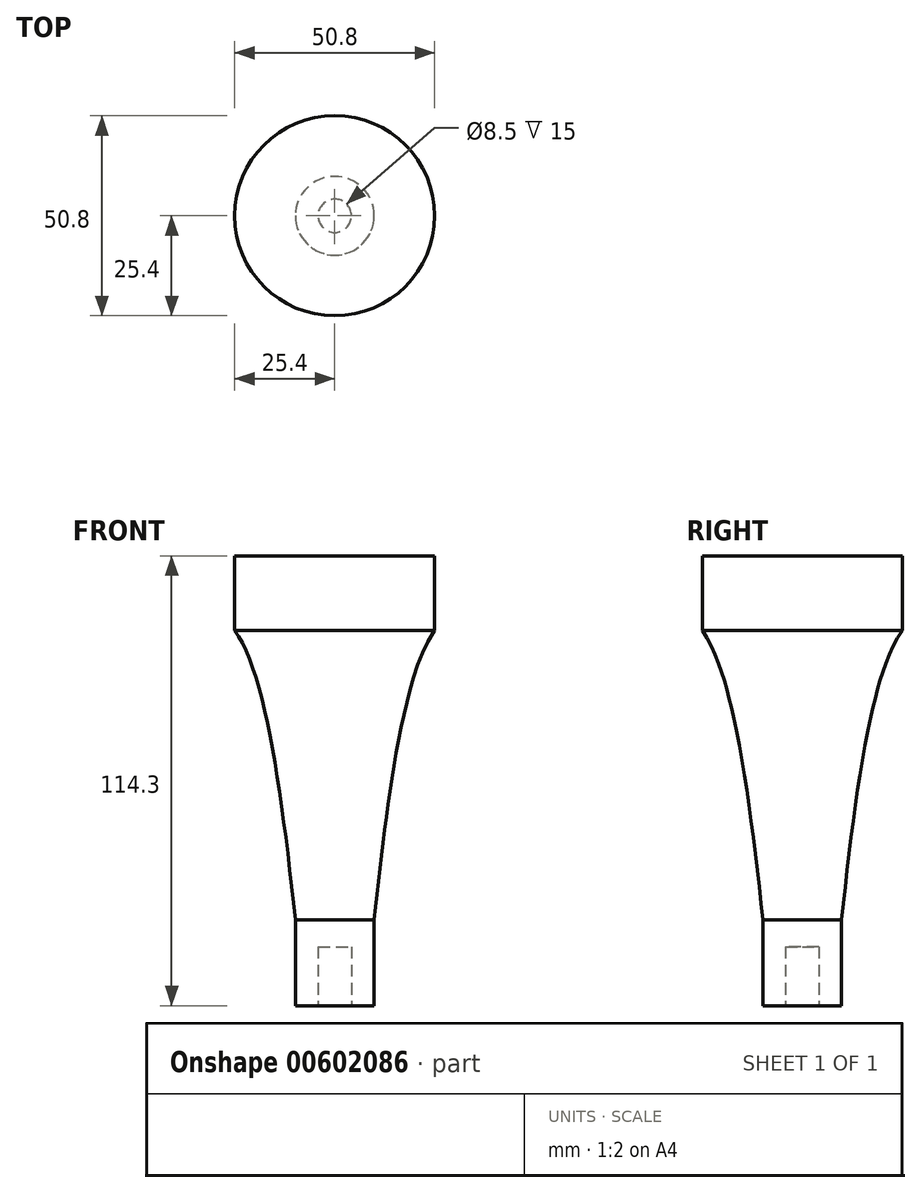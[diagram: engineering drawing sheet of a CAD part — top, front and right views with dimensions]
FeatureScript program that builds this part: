
annotation { "Feature Type Name" : "Feature", "Feature Type Description" : "" }
export const myFeature = defineFeature(function(context is Context, id is Id, definition is map)
    precondition{}
    {
        {
            var Q0;
            Q0=qCreatedBy(makeId("Top.planeOp"),FACE);
            var sketch = newSketch(context, id + "F0", { "sketchPlane" : qUnion([Q0])});
            skCircle(sketch, "E0", {"center": v(0, 0) * mm, "radius": 10 * mm});
            skSolve(sketch);
        }
        {
            var Q0;
            Q0 = qSketchRegion(id + "F0", true);
            extrude(context, id + "F1", {"entities" : qUnion([Q0]), "depth" : 101.6 * mm, "offsetDistance" : 25.4 * mm});
        }
        {
            var Q0;
            Q0=qCreatedBy(makeId("Front.planeOp"),FACE);
            var sketch = newSketch(context, id + "F2", { "sketchPlane" : qUnion([Q0])});
            skLineSegment(sketch, "E1.bottom", {"start": v(0, 0) * mm, "end": v(38.1, 0) * mm});
            skLineSegment(sketch, "E1.top", {"start": v(0, 101.6) * mm, "end": v(38.1, 101.6) * mm});
            skLineSegment(sketch, "E1.left", {"start": v(0, 0) * mm, "end": v(0, 101.6) * mm});
            skLineSegment(sketch, "E1.right", {"start": v(38.1, 0) * mm, "end": v(38.1, 101.6) * mm});
            skFitSpline(sketch, "E2", {"points": [v(38.1, 101.6) * mm, v(25.8, 95.89) * mm, v(7.77, 0) * mm], "startDerivative": vector(-48.1, -6) * mm, "endDerivative": vector(-17.25, -171.93) * mm});
            skSolve(sketch);
        }
        {
            var Q0;
            Q0=makeQuery(id+"F2.imprint","IMPRINT",FACE,{"disambiguationData":[TD([[makeQuery(id+"F2.imprint","IMPRINT",EDGE,{"derivedFrom":sQuery(id+"F2.wireOp",EDGE,"E1.top")}),-1.0]])]});
            var Q1;
            Q1=sQuery(id+"F2.wireOp",EDGE,"E1.left");
            revolve(context, id + "F3", {"operationType" : NewBodyOperationType.ADD, "entities" : qUnion([Q0]), "axis" : qUnion([Q1]), "revolveType" : RevolveType.FULL});
        }
        {
            var Q0;
            Q0=makeQuery(id+"F3.boolean.opBoolean","MERGE",FACE,{"derivedFrom":[makeQuery(id+"F1.opExtrude","CAP_FACE",FACE,{"disambiguationData":[OSD([sQuery(id+"F0.wireOp",EDGE,"E0")])],"isStart":false}),makeQuery(id+"F3.opRevolve","SWEPT_FACE",FACE,{"disambiguationData":[OSD([sQuery(id+"F2.wireOp",EDGE,"E1.top")])]})]});
            var sketch = newSketch(context, id + "F4", { "sketchPlane" : qUnion([Q0])});
            skSolve(sketch);
        }
        {
            var Q0;
            Q0 = qSketchRegion(id + "F4", true);
            var Q1;
            Q1=makeQuery(id+"F4.imprint","IMPRINT",FACE,{"disambiguationData":[TD([[makeQuery(id+"F4.imprint","IMPRINT",EDGE,{"derivedFrom":makeQuery(id+"F3.opRevolve","SWEPT_EDGE",EDGE,{"disambiguationData":[OSD([sQuery(id+"F2.wireOp",EDGE,"E1.top"),sQuery(id+"F2.wireOp",EDGE,"E1.right"),sQuery(id+"F2.wireOp",EDGE,"E2")])]})}),-1.0]])]});
            extrude(context, id + "F5", {"entities" : qUnion([Q0, Q1]), "operationType" : NewBodyOperationType.ADD, "depth" : 12.7 * mm, "offsetDistance" : 25.4 * mm});
        }
        {
            var Q0;
            Q0=makeQuery(id+"F1.opExtrude","CAP_FACE",FACE,{"disambiguationData":[OSD([sQuery(id+"F0.wireOp",EDGE,"E0")])],"isStart":true});
            var sketch = newSketch(context, id + "F6", { "sketchPlane" : qUnion([Q0])});
            skCircle(sketch, "E3", {"center": v(0, 0) * mm, "radius": 4.25 * mm});
            skSolve(sketch);
        }
        {
            var Q0;
            Q0 = qSketchRegion(id + "F6", true);
            extrude(context, id + "F7", {"entities" : qUnion([Q0]), "operationType" : NewBodyOperationType.REMOVE, "oppositeDirection" : true, "depth" : 15 * mm, "offsetDistance" : 25.4 * mm});
        }
        {
            var Q0;
            Q0=makeQuery(id+"F5.opExtrude","CAP_FACE",FACE,{"disambiguationData":[OSD([sQuery(id+"F2.wireOp",EDGE,"E1.top"),sQuery(id+"F2.wireOp",EDGE,"E1.right"),sQuery(id+"F2.wireOp",EDGE,"E2")])],"isStart":false});
            var sketch = newSketch(context, id + "F8", { "sketchPlane" : qUnion([Q0])});
            skCircle(sketch, "E4", {"center": v(0, 0) * mm, "radius": 25.4 * mm});
            skSolve(sketch);
        }
        {
            var Q0;
            Q0=makeQuery(id+"F8.imprint","IMPRINT",FACE,{"disambiguationData":[TD([[makeQuery(id+"F8.imprint","IMPRINT",EDGE,{"derivedFrom":sQuery(id+"F8.wireOp",EDGE,"E4")}),-1.0]])]});
            extrude(context, id + "F9", {"entities" : qUnion([Q0]), "operationType" : NewBodyOperationType.REMOVE, "oppositeDirection" : true, "depth" : 25.4 * mm, "offsetDistance" : 25.4 * mm});
        }
    });
